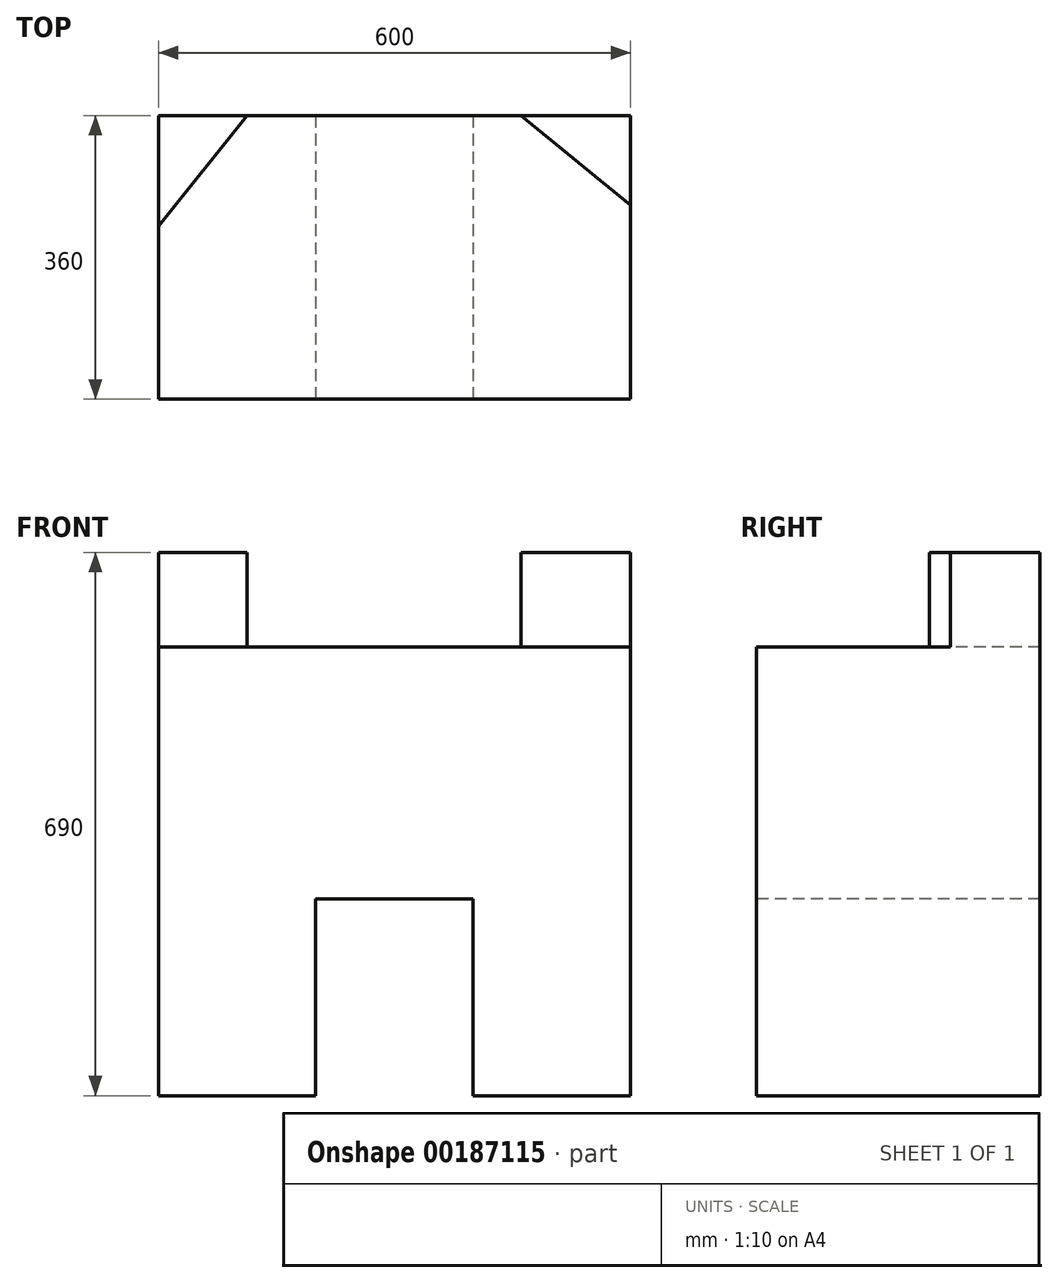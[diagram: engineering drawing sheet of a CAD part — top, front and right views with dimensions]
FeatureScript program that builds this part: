
annotation { "Feature Type Name" : "Feature", "Feature Type Description" : "" }
export const myFeature = defineFeature(function(context is Context, id is Id, definition is map)
    precondition{}
    {
        {
            var Q0;
            Q0=qCreatedBy(makeId("Top.planeOp"),FACE);
            var sketch = newSketch(context, id + "F0", { "sketchPlane" : qUnion([Q0])});
            skLineSegment(sketch, "E0.bottom", {"start": v(300, 180) * mm, "end": v(-300, 180) * mm});
            skLineSegment(sketch, "E0.top", {"start": v(300, -180) * mm, "end": v(-300, -180) * mm});
            skLineSegment(sketch, "E0.left", {"start": v(300, 180) * mm, "end": v(300, -180) * mm});
            skLineSegment(sketch, "E0.right", {"start": v(-300, 180) * mm, "end": v(-300, -180) * mm});
            skPoint(sketch, "E0.middle", {"position": v(0, 0) * mm});
            skSolve(sketch);
        }
        {
            var Q0;
            Q0 = qSketchRegion(id + "F0", true);
            extrude(context, id + "F1", {"entities" : qUnion([Q0]), "depth" : 570 * mm});
        }
        {
            var Q0;
            Q0=makeQuery(id+"F1.opExtrude","CAP_FACE",FACE,{"disambiguationData":[OSD([sQuery(id+"F0.wireOp",EDGE,"E0.bottom"),sQuery(id+"F0.wireOp",EDGE,"E0.top"),sQuery(id+"F0.wireOp",EDGE,"E0.left"),sQuery(id+"F0.wireOp",EDGE,"E0.right")])],"isStart":false});
            var sketch = newSketch(context, id + "F2", { "sketchPlane" : qUnion([Q0])});
            skLineSegment(sketch, "E1", {"start": v(160.51, 180) * mm, "end": v(300, 66.23) * mm});
            skLineSegment(sketch, "E2", {"start": v(-187.38, 180) * mm, "end": v(-300, 39.59) * mm});
            skSolve(sketch);
        }
        {
            var Q0;
            {var subQ0=sQuery(id+"F2.wireOp",EDGE,"E2");Q0=makeQuery(id+"F2.imprint","IMPRINT",FACE,{"disambiguationData":[TD([[makeQuery(id+"F2.imprint","IMPRINT",EDGE,{"derivedFrom":subQ0}),-1.0]])]});}
            var Q1;
            {var subQ0=sQuery(id+"F2.wireOp",EDGE,"E1");Q1=makeQuery(id+"F2.imprint","IMPRINT",FACE,{"disambiguationData":[TD([[makeQuery(id+"F2.imprint","IMPRINT",EDGE,{"derivedFrom":subQ0}),1.0]])]});}
            extrude(context, id + "F3", {"entities" : qUnion([Q0, Q1]), "operationType" : NewBodyOperationType.ADD, "depth" : 120 * mm});
        }
        {
            var Q0;
            Q0=makeQuery(id+"F1.opExtrude","SWEPT_FACE",FACE,{"disambiguationData":[OSD([sQuery(id+"F0.wireOp",EDGE,"E0.top")])]});
            var sketch = newSketch(context, id + "F4", { "sketchPlane" : qUnion([Q0])});
            skLineSegment(sketch, "E3.bottom", {"start": v(0, 125) * mm, "end": v(0, 125) * mm});
            skLineSegment(sketch, "E3.top", {"start": v(0, -125) * mm, "end": v(0, -125) * mm});
            skLineSegment(sketch, "E3.left", {"start": v(0, 0) * mm, "end": v(0, -125) * mm});
            skPoint(sketch, "E3.middle", {"position": v(0, 0) * mm});
            skLineSegment(sketch, "E4.bottom", {"start": v(100, 0) * mm, "end": v(-100, 0) * mm});
            skLineSegment(sketch, "E4.top", {"start": v(100, 250) * mm, "end": v(-100, 250) * mm});
            skLineSegment(sketch, "E4.left", {"start": v(100, 0) * mm, "end": v(100, 250) * mm});
            skLineSegment(sketch, "E4.right", {"start": v(-100, 0) * mm, "end": v(-100, 250) * mm});
            skPoint(sketch, "E4.middle", {"position": v(0, 125) * mm});
            skSolve(sketch);
        }
        {
            var Q0;
            Q0 = qSketchRegion(id + "F4", true);
            extrude(context, id + "F5", {"entities" : qUnion([Q0]), "operationType" : NewBodyOperationType.REMOVE, "endBound" : BoundingType.THROUGH_ALL, "oppositeDirection" : true, "depth" : 25 * mm});
        }
    });
